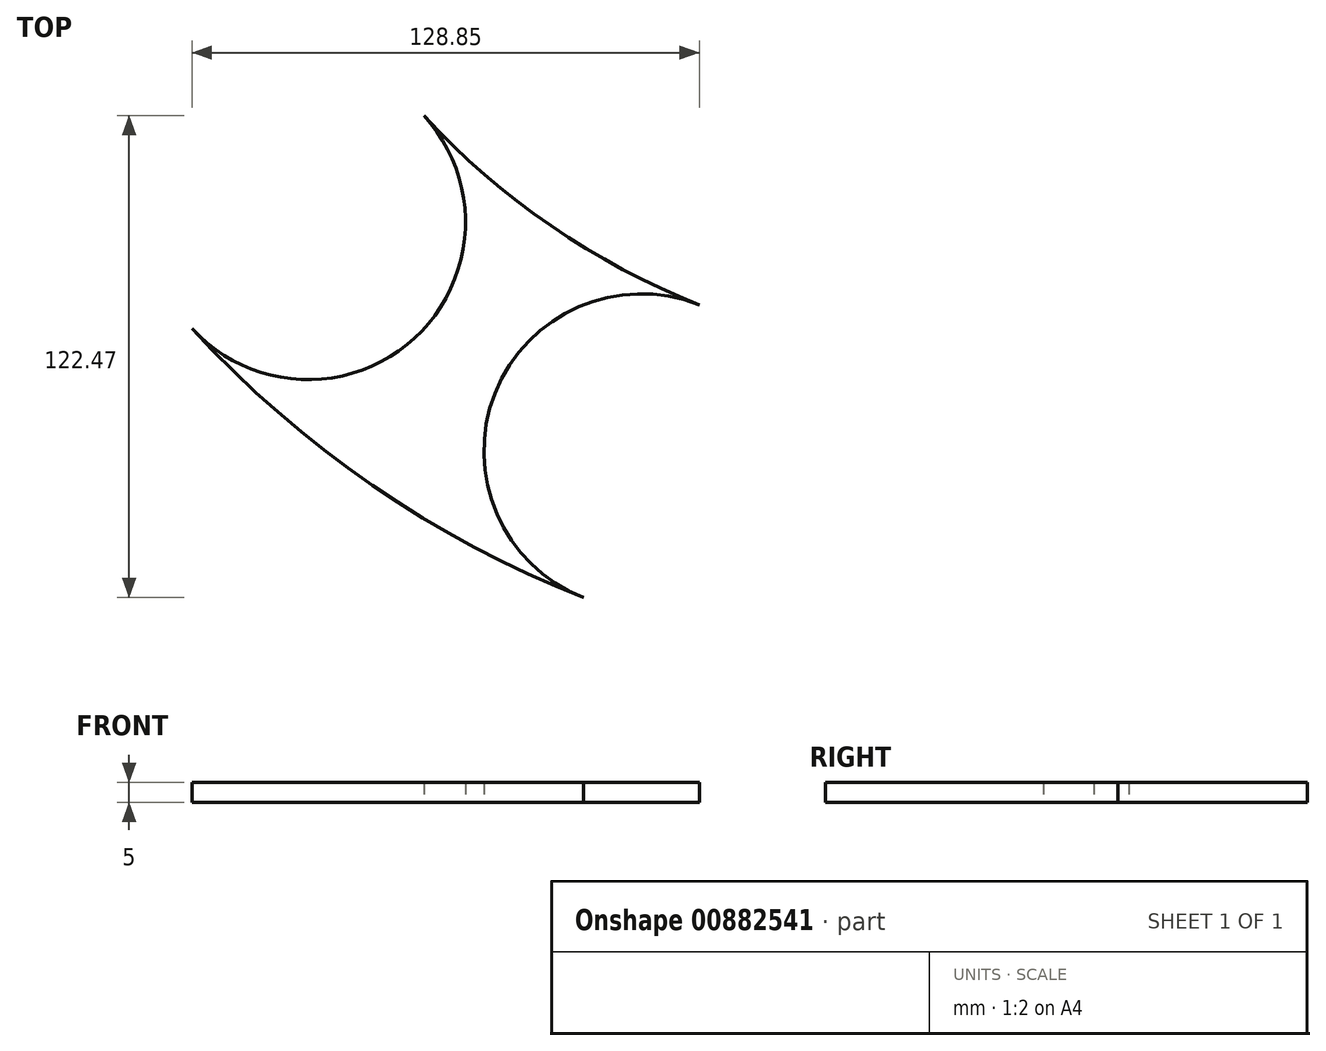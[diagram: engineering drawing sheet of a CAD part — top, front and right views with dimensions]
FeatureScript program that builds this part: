
annotation { "Feature Type Name" : "Feature", "Feature Type Description" : "" }
export const myFeature = defineFeature(function(context is Context, id is Id, definition is map)
    precondition{}
    {
        {
            var Q0;
            Q0=qCreatedBy(makeId("Top.planeOp"),FACE);
            var sketch = newSketch(context, id + "F0", { "sketchPlane" : qUnion([Q0])});
            skLineSegment(sketch, "E0.bottom", {"start": v(125, -125) * mm, "end": v(-125, -125) * mm});
            skLineSegment(sketch, "E0.top", {"start": v(125, 125) * mm, "end": v(-125, 125) * mm});
            skLineSegment(sketch, "E0.left", {"start": v(125, -125) * mm, "end": v(125, 125) * mm});
            skLineSegment(sketch, "E0.right", {"start": v(-125, -125) * mm, "end": v(-125, 125) * mm});
            skPoint(sketch, "E0.middle", {"position": v(0, 0) * mm});
            skLineSegment(sketch, "E1", {"start": v(0, 0) * mm, "end": v(-125, 0) * mm, "construction": true});
            skLineSegment(sketch, "E2.bottom", {"start": v(-349.96, 0) * mm, "end": v(0, 0) * mm});
            skLineSegment(sketch, "E2.left", {"start": v(-349.96, 0) * mm, "end": v(-349.96, 125) * mm});
            skLineSegment(sketch, "E2.right", {"start": v(125, 0) * mm, "end": v(125, 125) * mm});
            skLineSegment(sketch, "E3.MirrorCS", {"start": v(-349.96, 0) * mm, "end": v(-349.96, -249.62) * mm});
            skLineSegment(sketch, "E4.MirrorCS", {"start": v(-349.96, -249.62) * mm, "end": v(125, -249.62) * mm});
            skLineSegment(sketch, "E5.MirrorCS", {"start": v(125, 0) * mm, "end": v(125, -249.62) * mm});
            skLineSegment(sketch, "E6", {"start": v(-349.96, 125) * mm, "end": v(125, 125) * mm});
            skPoint(sketch, "E2.top.start.orphan", {"position": v(-349.96, 249.62) * mm});
            skPoint(sketch, "E7.orphan", {"position": v(125, 249.62) * mm});
            skLineSegment(sketch, "E8", {"start": v(-349.96, 29.15) * mm, "end": v(-125, 29.15) * mm});
            skLineSegment(sketch, "E9", {"start": v(-349.96, -249.62) * mm, "end": v(-349.96, -298.58) * mm});
            skLineSegment(sketch, "E10", {"start": v(-349.96, -298.58) * mm, "end": v(124.79, -298.58) * mm});
            skLineSegment(sketch, "E11", {"start": v(124.79, -298.58) * mm, "end": v(125, -249.62) * mm});
            skLineSegment(sketch, "E12", {"start": v(-294.72, 29.15) * mm, "end": v(-294.72, -298.58) * mm});
            skSolve(sketch);
        }
        {
            var Q0;
            {var subQ0=sQuery(id+"F0.wireOp",EDGE,"E8");var subQ1=sQuery(id+"F0.wireOp",EDGE,"E0.right");var subQ2=makeQuery(id+"F0.imprint","INTERSECT",VERTEX,{"derivedFrom":[subQ1,subQ0]});Q0=makeQuery(id+"F0.imprint","IMPRINT",FACE,{"disambiguationData":[TD([[makeQuery(id+"F0.imprint","IMPRINT",EDGE,{"disambiguationData":[TD([[subQ2,1.0]])],"derivedFrom":subQ1}),1.0]])]});}
            var Q1;
            {var subQ5=sQuery(id+"F0.wireOp",EDGE,"E0.bottom");Q1=makeQuery(id+"F0.imprint","IMPRINT",FACE,{"disambiguationData":[TD([[makeQuery(id+"F0.imprint","IMPRINT",EDGE,{"derivedFrom":subQ5}),1.0]])]});}
            var Q2;
            {var subQ0=sQuery(id+"F0.wireOp",EDGE,"E11");Q2=makeQuery(id+"F0.imprint","IMPRINT",FACE,{"disambiguationData":[TD([[makeQuery(id+"F0.imprint","IMPRINT",EDGE,{"derivedFrom":subQ0}),1.0]])]});}
            extrude(context, id + "F1", {"entities" : qUnion([Q0, Q1, Q2]), "depth" : 5 * mm, "offsetDistance" : 25 * mm});
        }
        {
            var Q0;
            Q0=makeQuery(id+"F1.opExtrude","CAP_FACE",FACE,{"disambiguationData":[OSD([sQuery(id+"F0.wireOp",EDGE,"E0.bottom"),sQuery(id+"F0.wireOp",EDGE,"E0.top"),sQuery(id+"F0.wireOp",EDGE,"E0.left"),sQuery(id+"F0.wireOp",EDGE,"E0.right"),sQuery(id+"F0.wireOp",EDGE,"E2.top"),sQuery(id+"F0.wireOp",EDGE,"E2.left"),sQuery(id+"F0.wireOp",EDGE,"E2.right"),sQuery(id+"F0.wireOp",EDGE,"E3.MirrorCS"),sQuery(id+"F0.wireOp",EDGE,"E4.MirrorCS"),sQuery(id+"F0.wireOp",EDGE,"E5.MirrorCS")])],"isStart":false});
            var sketch = newSketch(context, id + "F2", { "sketchPlane" : qUnion([Q0])});
            skCircle(sketch, "E13", {"center": v(0, 0) * mm, "radius": 270 * mm});
            skCircle(sketch, "E14", {"center": v(0, 0) * mm, "radius": 190 * mm});
            skLineSegment(sketch, "E15", {"start": v(0, 0) * mm, "end": v(-270, 0) * mm, "construction": true});
            skCircle(sketch, "E16", {"center": v(0, 0) * mm, "radius": 230 * mm, "construction": true});
            skCircle(sketch, "E17", {"center": v(-228.72, -24.2) * mm, "radius": 5 * mm});
            skCircle(sketch, "E18.1.0", {"center": v(-219.77, -67.83) * mm, "radius": 5 * mm});
            skCircle(sketch, "E18.2.0", {"center": v(-202.58, -108.9) * mm, "radius": 5 * mm});
            skCircle(sketch, "E18.3.0", {"center": v(-177.8, -145.9) * mm, "radius": 5 * mm});
            skCircle(sketch, "E18.4.0", {"center": v(-146.35, -177.43) * mm, "radius": 5 * mm});
            skCircle(sketch, "E18.5.0", {"center": v(-109.4, -202.31) * mm, "radius": 5 * mm});
            skCircle(sketch, "E18.6.0", {"center": v(-68.37, -219.6) * mm, "radius": 5 * mm});
            skCircle(sketch, "E18.7.0", {"center": v(-24.77, -228.66) * mm, "radius": 5 * mm});
            skCircle(sketch, "E18.8.0", {"center": v(19.76, -229.15) * mm, "radius": 5 * mm});
            skCircle(sketch, "E18.9.0", {"center": v(63.55, -221.05) * mm, "radius": 5 * mm});
            skLineSegment(sketch, "E18.anchor1", {"start": v(0, 0) * mm, "end": v(-228.72, -24.2) * mm, "construction": true});
            skLineSegment(sketch, "E18.anchor2", {"start": v(0, 0) * mm, "end": v(63.55, -221.05) * mm, "construction": true});
            skSolve(sketch);
        }
        {
            var Q0;
            Q0=makeQuery(id+"F2.imprint","IMPRINT",FACE,{"disambiguationData":[TD([[makeQuery(id+"F2.imprint","IMPRINT",EDGE,{"derivedFrom":sQuery(id+"F2.wireOp",EDGE,"E17")}),1.0]])]});
            var Q1;
            Q1=makeQuery(id+"F2.imprint","IMPRINT",FACE,{"disambiguationData":[TD([[makeQuery(id+"F2.imprint","IMPRINT",EDGE,{"derivedFrom":sQuery(id+"F2.wireOp",EDGE,"E18.1.0")}),1.0]])]});
            var Q2;
            Q2=makeQuery(id+"F2.imprint","IMPRINT",FACE,{"disambiguationData":[TD([[makeQuery(id+"F2.imprint","IMPRINT",EDGE,{"derivedFrom":sQuery(id+"F2.wireOp",EDGE,"E18.2.0")}),1.0]])]});
            var Q3;
            Q3=makeQuery(id+"F2.imprint","IMPRINT",FACE,{"disambiguationData":[TD([[makeQuery(id+"F2.imprint","IMPRINT",EDGE,{"derivedFrom":sQuery(id+"F2.wireOp",EDGE,"E18.3.0")}),1.0]])]});
            var Q4;
            Q4=makeQuery(id+"F2.imprint","IMPRINT",FACE,{"disambiguationData":[TD([[makeQuery(id+"F2.imprint","IMPRINT",EDGE,{"derivedFrom":sQuery(id+"F2.wireOp",EDGE,"E18.4.0")}),1.0]])]});
            var Q5;
            Q5=makeQuery(id+"F2.imprint","IMPRINT",FACE,{"disambiguationData":[TD([[makeQuery(id+"F2.imprint","IMPRINT",EDGE,{"derivedFrom":sQuery(id+"F2.wireOp",EDGE,"E18.5.0")}),1.0]])]});
            var Q6;
            Q6=makeQuery(id+"F2.imprint","IMPRINT",FACE,{"disambiguationData":[TD([[makeQuery(id+"F2.imprint","IMPRINT",EDGE,{"derivedFrom":sQuery(id+"F2.wireOp",EDGE,"E18.6.0")}),1.0]])]});
            var Q7;
            Q7=makeQuery(id+"F2.imprint","IMPRINT",FACE,{"disambiguationData":[TD([[makeQuery(id+"F2.imprint","IMPRINT",EDGE,{"derivedFrom":sQuery(id+"F2.wireOp",EDGE,"E18.7.0")}),1.0]])]});
            var Q8;
            Q8=makeQuery(id+"F2.imprint","IMPRINT",FACE,{"disambiguationData":[TD([[makeQuery(id+"F2.imprint","IMPRINT",EDGE,{"derivedFrom":sQuery(id+"F2.wireOp",EDGE,"E18.8.0")}),1.0]])]});
            var Q9;
            Q9=makeQuery(id+"F2.imprint","IMPRINT",FACE,{"disambiguationData":[TD([[makeQuery(id+"F2.imprint","IMPRINT",EDGE,{"derivedFrom":sQuery(id+"F2.wireOp",EDGE,"E18.9.0")}),1.0]])]});
            extrude(context, id + "F3", {"entities" : qUnion([Q0, Q1, Q2, Q3, Q4, Q5, Q6, Q7, Q8, Q9]), "operationType" : NewBodyOperationType.REMOVE, "endBound" : BoundingType.THROUGH_ALL, "oppositeDirection" : true, "depth" : 6 * mm, "offsetDistance" : 25 * mm});
        }
        {
            var Q0;
            Q0=makeQuery(id+"F1.opExtrude","CAP_FACE",FACE,{"disambiguationData":[OSD([sQuery(id+"F0.wireOp",EDGE,"E0.bottom"),sQuery(id+"F0.wireOp",EDGE,"E0.right"),sQuery(id+"F0.wireOp",EDGE,"E5.MirrorCS"),sQuery(id+"F0.wireOp",EDGE,"E8"),sQuery(id+"F0.wireOp",EDGE,"E10"),sQuery(id+"F0.wireOp",EDGE,"E11"),sQuery(id+"F0.wireOp",EDGE,"E12")])],"isStart":false});
            var sketch = newSketch(context, id + "F4", { "sketchPlane" : qUnion([Q0])});
            skCircle(sketch, "E19", {"center": v(0, 0) * mm, "radius": 295 * mm});
            skLineSegment(sketch, "E20", {"start": v(178.33, -235) * mm, "end": v(178.33, -361.67) * mm});
            skLineSegment(sketch, "E21", {"start": v(178.33, -361.67) * mm, "end": v(-429.48, -361.67) * mm});
            skLineSegment(sketch, "E22", {"start": v(-429.48, -361.67) * mm, "end": v(-429.48, 76.22) * mm});
            skLineSegment(sketch, "E23", {"start": v(-429.48, 76.22) * mm, "end": v(-284.98, 76.22) * mm});
            skSolve(sketch);
        }
        {
            var Q0;
            {var subQ0=sQuery(id+"F4.wireOp",EDGE,"E19");var subQ1=makeQuery(id+"F1.opExtrude","CAP_EDGE",EDGE,{"disambiguationData":[OSD([sQuery(id+"F0.wireOp",EDGE,"E12")])],"isStart":false});var subQ2=makeQuery(id+"F4.imprint","INTERSECT",VERTEX,{"disambiguationData":[OD(0.0)],"derivedFrom":[subQ1,subQ0]});Q0=makeQuery(id+"F4.imprint","IMPRINT",FACE,{"disambiguationData":[TD([[makeQuery(id+"F4.imprint","IMPRINT",EDGE,{"disambiguationData":[TD([[subQ2,-1.0]])],"derivedFrom":subQ0}),1.0]])]});}
            var Q1;
            {var subQ0=sQuery(id+"F4.wireOp",EDGE,"E19");var subQ1=makeQuery(id+"F1.opExtrude","CAP_EDGE",EDGE,{"disambiguationData":[OSD([sQuery(id+"F0.wireOp",EDGE,"E8")])],"isStart":false});var subQ2=makeQuery(id+"F4.imprint","INTERSECT",VERTEX,{"derivedFrom":[subQ1,subQ0]});Q1=makeQuery(id+"F4.imprint","IMPRINT",FACE,{"disambiguationData":[TD([[makeQuery(id+"F4.imprint","IMPRINT",EDGE,{"disambiguationData":[TD([[subQ2,-1.0]])],"derivedFrom":subQ0}),-1.0]])]});}
            var Q2;
            {var subQ11=sQuery(id+"F4.wireOp",EDGE,"E20");Q2=makeQuery(id+"F4.imprint","IMPRINT",FACE,{"disambiguationData":[TD([[makeQuery(id+"F4.imprint","IMPRINT",EDGE,{"derivedFrom":subQ11}),-1.0]])]});}
            var Q3;
            {var subQ5=makeQuery(id+"F1.opExtrude","CAP_EDGE",EDGE,{"disambiguationData":[OSD([sQuery(id+"F0.wireOp",EDGE,"E10")])],"isStart":false});Q3=makeQuery(id+"F4.imprint","IMPRINT",FACE,{"disambiguationData":[TD([[makeQuery(id+"F4.imprint","IMPRINT",EDGE,{"derivedFrom":subQ5}),1.0]])]});}
            extrude(context, id + "F5", {"entities" : qUnion([Q0, Q1, Q2, Q3]), "operationType" : NewBodyOperationType.REMOVE, "oppositeDirection" : true, "depth" : 25 * mm, "offsetDistance" : 25 * mm});
        }
        {
            var Q0;
            Q0=makeQuery(id+"F1.opExtrude","CAP_FACE",FACE,{"disambiguationData":[OSD([sQuery(id+"F0.wireOp",EDGE,"E0.bottom"),sQuery(id+"F0.wireOp",EDGE,"E0.right"),sQuery(id+"F0.wireOp",EDGE,"E5.MirrorCS"),sQuery(id+"F0.wireOp",EDGE,"E8"),sQuery(id+"F0.wireOp",EDGE,"E10"),sQuery(id+"F0.wireOp",EDGE,"E11"),sQuery(id+"F0.wireOp",EDGE,"E12")])],"isStart":false});
            var sketch = newSketch(context, id + "F6", { "sketchPlane" : qUnion([Q0])});
            skCircle(sketch, "E24", {"center": v(0, 0) * mm, "radius": 230 * mm, "construction": true});
            skCircle(sketch, "E25", {"center": v(-169.32, -155.67) * mm, "radius": 40 * mm});
            skCircle(sketch, "E26", {"center": v(-84.63, -213.86) * mm, "radius": 40 * mm});
            skCircle(sketch, "E27", {"center": v(0, 0) * mm, "radius": 190 * mm});
            skCircle(sketch, "E28", {"center": v(0, 0) * mm, "radius": 270 * mm});
            skSolve(sketch);
        }
        {
            var Q0;
            Q0=makeQuery(id+"F6.imprint","IMPRINT",FACE,{"disambiguationData":[TD([[makeQuery(id+"F6.imprint","IMPRINT",EDGE,{"derivedFrom":makeQuery(id+"F3.boolean.opBoolean","COPY",EDGE,{"derivedFrom":makeQuery(id+"F3.opExtrude","CAP_EDGE",EDGE,{"disambiguationData":[OSD([sQuery(id+"F2.wireOp",EDGE,"E18.5.0")])],"isStart":true})})}),-1.0]])]});
            var Q1;
            {var subQ0=sQuery(id+"F6.wireOp",EDGE,"E27");var subQ1=sQuery(id+"F6.wireOp",EDGE,"E25");var subQ2=makeQuery(id+"F6.imprint","INTERSECT",VERTEX,{"derivedFrom":[subQ1,subQ0]});Q1=makeQuery(id+"F6.imprint","IMPRINT",FACE,{"disambiguationData":[TD([[makeQuery(id+"F6.imprint","IMPRINT",EDGE,{"disambiguationData":[TD([[subQ2,1.0]])],"derivedFrom":subQ1}),-1.0]])]});}
            var Q2;
            Q2=makeQuery(id+"F6.imprint","IMPRINT",FACE,{"disambiguationData":[TD([[makeQuery(id+"F6.imprint","IMPRINT",EDGE,{"derivedFrom":makeQuery(id+"F3.boolean.opBoolean","COPY",EDGE,{"derivedFrom":makeQuery(id+"F3.opExtrude","CAP_EDGE",EDGE,{"disambiguationData":[OSD([sQuery(id+"F2.wireOp",EDGE,"E18.3.0")])],"isStart":true})})}),-1.0]])]});
            var Q3;
            Q3=makeQuery(id+"F6.imprint","IMPRINT",FACE,{"disambiguationData":[TD([[makeQuery(id+"F6.imprint","IMPRINT",EDGE,{"derivedFrom":makeQuery(id+"F3.boolean.opBoolean","COPY",EDGE,{"derivedFrom":makeQuery(id+"F3.opExtrude","CAP_EDGE",EDGE,{"disambiguationData":[OSD([sQuery(id+"F2.wireOp",EDGE,"E18.5.0")])],"isStart":true})})}),1.0]])]});
            var Q4;
            Q4=makeQuery(id+"F6.imprint","IMPRINT",FACE,{"disambiguationData":[TD([[makeQuery(id+"F6.imprint","IMPRINT",EDGE,{"derivedFrom":makeQuery(id+"F3.boolean.opBoolean","COPY",EDGE,{"derivedFrom":makeQuery(id+"F3.opExtrude","CAP_EDGE",EDGE,{"disambiguationData":[OSD([sQuery(id+"F2.wireOp",EDGE,"E18.4.0")])],"isStart":true})})}),1.0]])]});
            extrude(context, id + "F7", {"entities" : qUnion([Q0, Q1, Q2, Q3, Q4]), "depth" : 5 * mm, "offsetDistance" : 25 * mm});
        }
        {
            var Q0;
            Q0=makeQuery(id+"F1.opExtrude","SWEPT_BODY",BODY,{"disambiguationData":[OSD([sQuery(id+"F0.wireOp",EDGE,"E0.bottom"),sQuery(id+"F0.wireOp",EDGE,"E0.right"),sQuery(id+"F0.wireOp",EDGE,"E5.MirrorCS"),sQuery(id+"F0.wireOp",EDGE,"E8"),sQuery(id+"F0.wireOp",EDGE,"E10"),sQuery(id+"F0.wireOp",EDGE,"E11"),sQuery(id+"F0.wireOp",EDGE,"E12")])]});
            deleteBodies(context, id + "F8", {"entities" : qUnion([Q0])});
        }
    });
